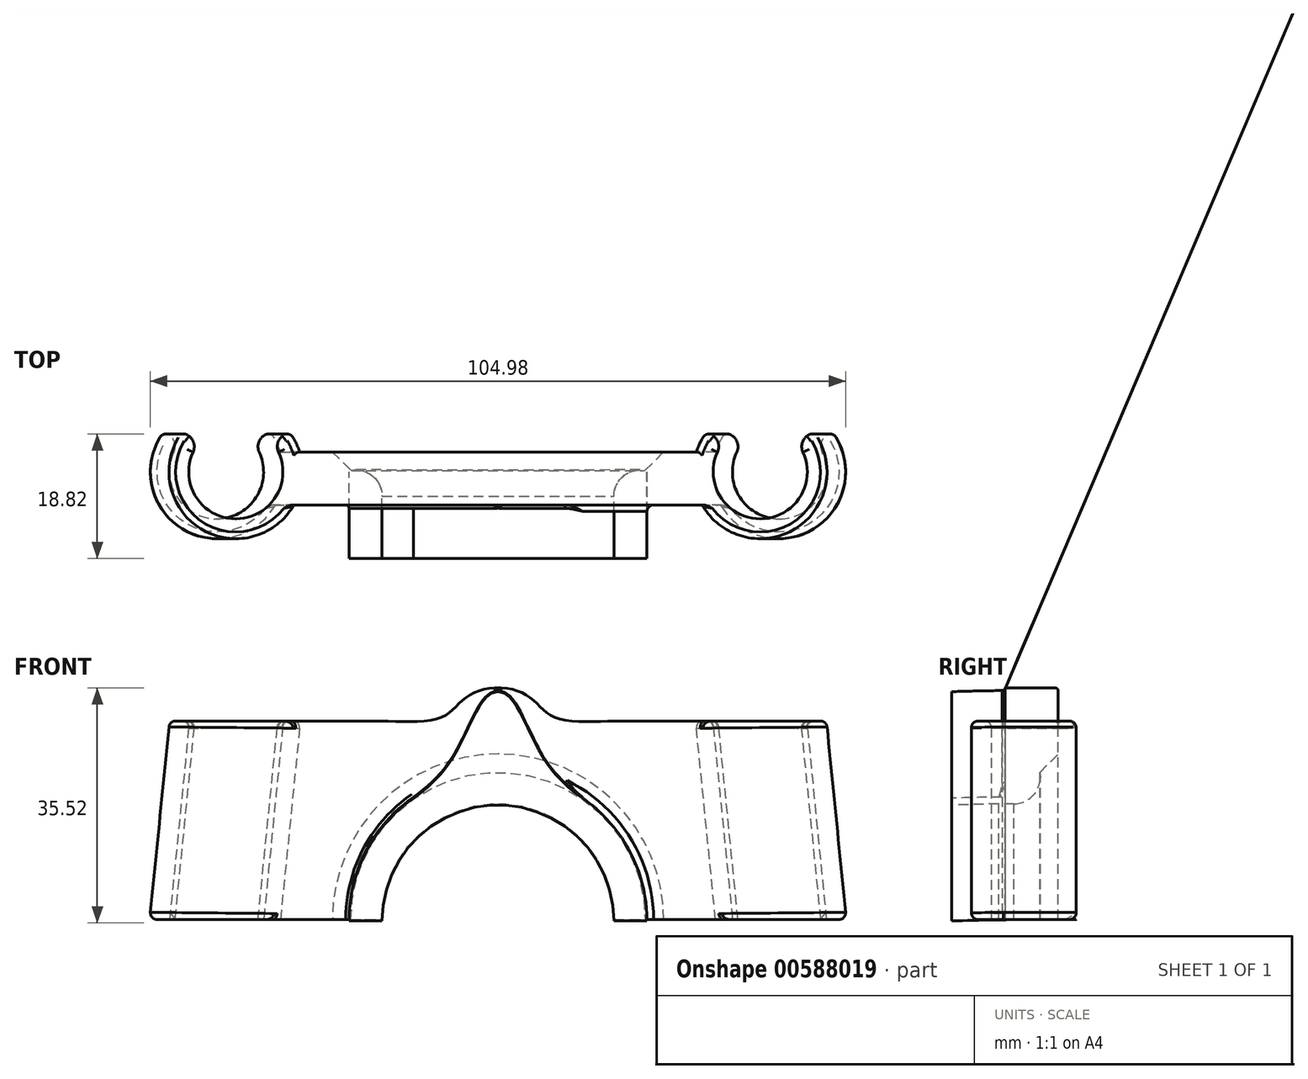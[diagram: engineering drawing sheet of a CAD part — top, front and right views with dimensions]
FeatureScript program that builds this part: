
annotation { "Feature Type Name" : "Feature", "Feature Type Description" : "" }
export const myFeature = defineFeature(function(context is Context, id is Id, definition is map)
    precondition{}
    {
        {
            var Q0;
            Q0=qCreatedBy(makeId("Front.planeOp"),FACE);
            var sketch = newSketch(context, id + "F0", { "sketchPlane" : qUnion([Q0])});
            skLineSegment(sketch, "E0", {"start": v(42.5, 0) * mm, "end": v(39.5, 30) * mm});
            skLineSegment(sketch, "E1", {"start": v(0, 48.67) * mm, "end": v(0, 0) * mm, "construction": true});
            skSolve(sketch);
        }
        {
            var Q0;
            Q0=qCreatedBy(makeId("Top.planeOp"),FACE);
            var sketch = newSketch(context, id + "F1", { "sketchPlane" : qUnion([Q0])});
            skArc(sketch, "E2", {"start": v(36.87, 4.32) * mm, "mid": v(42.5, -7.1) * mm, "end": v(48.13, 4.32) * mm});
            skArc(sketch, "E3.0", {"start": v(34.49, 6.15) * mm, "mid": v(42.5, -10.1) * mm, "end": v(50.51, 6.15) * mm});
            skLineSegment(sketch, "E4", {"start": v(48.13, 4.32) * mm, "end": v(50.51, 6.15) * mm});
            skLineSegment(sketch, "E5", {"start": v(36.87, 4.32) * mm, "end": v(34.49, 6.15) * mm});
            skLineSegment(sketch, "E6", {"start": v(42.5, 0) * mm, "end": v(42.5, 10.1) * mm, "construction": true});
            skLineSegment(sketch, "E7", {"start": v(36.87, 4.32) * mm, "end": v(42.5, 0) * mm, "construction": true});
            skSolve(sketch);
        }
        {
            var Q0;
            Q0 = qSketchRegion(id + "F1", true);
            var Q1;
            Q1=sQuery(id+"F0.wireOp",EDGE,"E0");
            sweep(context, id + "F2", {"profiles" : qUnion([Q0]), "path" : qUnion([Q1]), "keepProfileOrientation" : true});
        }
        {
            var Q0;
            Q0=qCreatedBy(makeId("Right.planeOp"),FACE);
            var sketch = newSketch(context, id + "F3", { "sketchPlane" : qUnion([Q0])});
            skCircle(sketch, "E8", {"center": v(0, -406) * mm, "radius": 406 * mm});
            skSolve(sketch);
        }
        {
            var Q0;
            Q0=makeQuery(id+"F2.opSweep","SWEPT_BODY",BODY,{"disambiguationData":[OSD([sQuery(id+"F0.wireOp",EDGE,"E0"),sQuery(id+"F1.wireOp",EDGE,"E2"),sQuery(id+"F1.wireOp",EDGE,"E3.0"),sQuery(id+"F1.wireOp",EDGE,"E4"),sQuery(id+"F1.wireOp",EDGE,"E5")])]});
            var Q1;
            Q1=qCreatedBy(makeId("Right.planeOp"),FACE);
            mirror(context, id + "F4", {"entities" : qUnion([Q0]), "mirrorPlane" : qUnion([Q1])});
        }
        {
            var Q0;
            Q0=qCreatedBy(makeId("Front.planeOp"),FACE);
            var sketch = newSketch(context, id + "F5", { "sketchPlane" : qUnion([Q0])});
            skArc(sketch, "E9", {"start": v(17.5, 0) * mm, "mid": v(0, 17.5) * mm, "end": v(-17.5, 0) * mm});
            skArc(sketch, "E10.0", {"start": v(22.5, 0) * mm, "mid": v(19.91, 10.48) * mm, "end": v(12.74, 18.54) * mm});
            skLineSegment(sketch, "E11", {"start": v(-22.5, 0) * mm, "end": v(-17.5, 0) * mm});
            skLineSegment(sketch, "E12", {"start": v(17.5, 0) * mm, "end": v(22.5, 0) * mm});
            skFitSpline(sketch, "E13", {"points": [v(12.74, 18.54) * mm, v(6.7, 24.92) * mm, v(2.82, 32.43) * mm, v(0, 34.64) * mm], "startDerivative": vector(-21.82, 15.7) * mm, "endDerivative": vector(-15.88, 1.73) * mm});
            skLineSegment(sketch, "E14", {"start": v(0, 0) * mm, "end": v(0, 35.45) * mm, "construction": true});
            skFitSpline(sketch, "E15.MirrorCS", {"points": [v(-12.74, 18.54) * mm, v(-6.7, 24.92) * mm, v(-2.82, 32.43) * mm, v(0, 34.64) * mm], "startDerivative": vector(21.82, 15.7) * mm, "endDerivative": vector(15.88, 1.73) * mm});
            skArc(sketch, "E16.trimOffspring", {"start": v(-12.74, 18.54) * mm, "mid": v(-19.91, 10.48) * mm, "end": v(-22.5, 0) * mm});
            skSolve(sketch);
        }
        {
            var Q0;
            Q0=qCreatedBy(makeId("Front.planeOp"),FACE);
            var sketch = newSketch(context, id + "F6", { "sketchPlane" : qUnion([Q0])});
            skLineSegment(sketch, "E17", {"start": v(0, 0) * mm, "end": v(0, 43.53) * mm, "construction": true});
            skArc(sketch, "E18", {"start": v(20, 0) * mm, "mid": v(0, 20) * mm, "end": v(-20, 0) * mm});
            skLineSegment(sketch, "E19.MirrorCS", {"start": v(-31.49, 30) * mm, "end": v(-18.64, 30) * mm});
            skFitSpline(sketch, "E20.MirrorCS", {"points": [v(0, 35.01) * mm, v(-5.21, 33.25) * mm, v(-8.7, 30.5) * mm, v(-18.64, 30) * mm], "startDerivative": vector(-19.82, 0.89) * mm, "endDerivative": vector(-23.26, 0) * mm});
            skLineSegment(sketch, "E21.MirrorCS", {"start": v(-34.49, 0) * mm, "end": v(-20, 0) * mm});
            skLineSegment(sketch, "E22.MirrorCS", {"start": v(-34.49, 0) * mm, "end": v(-31.49, 30) * mm});
            skLineSegment(sketch, "E23.MirrorCS", {"start": v(34.49, 0) * mm, "end": v(20, 0) * mm});
            skFitSpline(sketch, "E24.MirrorCS", {"points": [v(0, 35.01) * mm, v(5.21, 33.25) * mm, v(8.7, 30.5) * mm, v(18.64, 30) * mm], "startDerivative": vector(19.82, 0.89) * mm, "endDerivative": vector(23.26, 0) * mm});
            skLineSegment(sketch, "E25.MirrorCS", {"start": v(34.49, 0) * mm, "end": v(31.49, 30) * mm});
            skLineSegment(sketch, "E26.MirrorCS", {"start": v(31.49, 30) * mm, "end": v(18.64, 30) * mm});
            skSolve(sketch);
        }
        {
            var Q0;
            Q0 = qSketchRegion(id + "F6", true);
            extrude(context, id + "F7", {"entities" : qUnion([Q0]), "operationType" : NewBodyOperationType.ADD, "depth" : 5 * mm, "offsetDistance" : 25 * mm, "hasSecondDirection" : true, "secondDirectionOppositeDirection" : true, "secondDirectionDepth" : 3 * mm});
        }
        {
            var Q0;
            Q0=makeQuery(id+"F5.imprint","IMPRINT",FACE,{"disambiguationData":[TD([[makeQuery(id+"F5.imprint","IMPRINT",EDGE,{"derivedFrom":sQuery(id+"F5.wireOp",EDGE,"E9")}),-1.0]])]});
            var Q1;
            Q1=sQuery(id+"F3.wireOp",EDGE,"E8");
            revolve(context, id + "F8", {"operationType" : NewBodyOperationType.ADD, "entities" : qUnion([Q0]), "axis" : qUnion([Q1]), "revolveType" : RevolveType.ONE_DIRECTION, "angle" : 40 * degree});
        }
        {
            var Q0;
            Q0=makeQuery(id+"F8.opRevolve","CAP_EDGE",EDGE,{"disambiguationData":[OSD([sQuery(id+"F5.wireOp",EDGE,"E11")])],"isStart":false});
            chamfer(context, id + "F9", {"entities" : qUnion([Q0]), "width" : 30 * mm, "tangentPropagation" : true});
        }
        {
            var Q0;
            Q0=makeQuery(id+"F8.opRevolve","CAP_EDGE",EDGE,{"disambiguationData":[OSD([sQuery(id+"F5.wireOp",EDGE,"E9")])],"isStart":false});
            var Q1;
            Q1=makeQuery(id+"F8.opRevolve","CAP_EDGE",EDGE,{"disambiguationData":[OSD([sQuery(id+"F5.wireOp",EDGE,"E9")])],"isStart":true});
            fillet(context, id + "F10", {"entities" : qUnion([Q0, Q1]), "radius" : 4 * mm, "tangentPropagation" : true, "allowEdgeOverflow" : false});
        }
        {
            var Q0;
            Q0=makeQuery(id+"F2.opSweep","SWEPT_EDGE",EDGE,{"disambiguationData":[OSD([sQuery(id+"F0.wireOp",EDGE,"E0"),sQuery(id+"F1.wireOp",EDGE,"E2"),sQuery(id+"F1.wireOp",EDGE,"E5")])]});
            var Q1;
            Q1=makeQuery(id+"F2.opSweep","SWEPT_EDGE",EDGE,{"disambiguationData":[OSD([sQuery(id+"F0.wireOp",EDGE,"E0"),sQuery(id+"F1.wireOp",EDGE,"E2"),sQuery(id+"F1.wireOp",EDGE,"E4")])]});
            var Q2;
            Q2=makeQuery(id+"F4.opPattern","COPY",EDGE,{"derivedFrom":makeQuery(id+"F2.opSweep","SWEPT_EDGE",EDGE,{"disambiguationData":[OSD([sQuery(id+"F0.wireOp",EDGE,"E0"),sQuery(id+"F1.wireOp",EDGE,"E2"),sQuery(id+"F1.wireOp",EDGE,"E4")])]}),"instanceName":"1"});
            var Q3;
            Q3=makeQuery(id+"F4.opPattern","COPY",EDGE,{"derivedFrom":makeQuery(id+"F2.opSweep","SWEPT_EDGE",EDGE,{"disambiguationData":[OSD([sQuery(id+"F0.wireOp",EDGE,"E0"),sQuery(id+"F1.wireOp",EDGE,"E2"),sQuery(id+"F1.wireOp",EDGE,"E5")])]}),"instanceName":"1"});
            fillet(context, id + "F11", {"entities" : qUnion([Q0, Q1, Q2, Q3]), "radius" : 2 * mm, "tangentPropagation" : true, "allowEdgeOverflow" : false});
        }
        {
            var Q0;
            {var subQ1=sQuery(id+"F1.wireOp",EDGE,"E4");var subQ2=sQuery(id+"F0.wireOp",EDGE,"E0");var subQ3=sQuery(id+"F1.wireOp",EDGE,"E3.0");var subQ4=sQuery(id+"F0.wireOp",VERTEX,"E0.end");Q0=makeQuery(id+"F7.boolean.opBoolean","SPLIT",EDGE,{"disambiguationData":[TD([makeQuery(id+"F4.opPattern","COPY",FACE,{"derivedFrom":makeQuery(id+"F2.opSweep","SWEPT_FACE",FACE,{"disambiguationData":[OSD([subQ2,subQ1])]}),"instanceName":"1"})])],"derivedFrom":makeQuery(id+"F4.opPattern","COPY",EDGE,{"derivedFrom":makeQuery(id+"F2.opSweep","CAP_EDGE",EDGE,{"disambiguationData":[OSD([subQ4,subQ3])],"isStart":false}),"instanceName":"1"})});}
            var Q1;
            {var subQ0=sQuery(id+"F1.wireOp",EDGE,"E5");var subQ1=sQuery(id+"F0.wireOp",EDGE,"E0");var subQ2=sQuery(id+"F1.wireOp",EDGE,"E2");var subQ5=sQuery(id+"F1.wireOp",EDGE,"E4");var subQ6=sQuery(id+"F0.wireOp",VERTEX,"E0.end");var subQ9=makeQuery(id+"F4.opPattern","COPY",EDGE,{"derivedFrom":makeQuery(id+"F2.opSweep","CAP_EDGE",EDGE,{"disambiguationData":[OSD([subQ6,subQ2])],"isStart":false}),"instanceName":"1"});Q1=makeQuery(id+"Fb2eIdGMMGndcXa_1.opDeleteFace","MERGE",EDGE,{"derivedFrom":[makeQuery(id+"F7.boolean.opBoolean","SPLIT",EDGE,{"disambiguationData":[TD([makeQuery(id+"F4.opPattern","COPY",FACE,{"derivedFrom":makeQuery(id+"F2.opSweep","SWEPT_FACE",FACE,{"disambiguationData":[OSD([subQ1,subQ5])]}),"instanceName":"1"})])],"derivedFrom":subQ9}),makeQuery(id+"F7.boolean.opBoolean","SPLIT",EDGE,{"disambiguationData":[TD([makeQuery(id+"F4.opPattern","COPY",FACE,{"derivedFrom":makeQuery(id+"F2.opSweep","SWEPT_FACE",FACE,{"disambiguationData":[OSD([subQ1,subQ0])]}),"instanceName":"1"})])],"derivedFrom":subQ9})]});}
            var Q2;
            {var subQ0=sQuery(id+"F1.wireOp",EDGE,"E5");var subQ1=sQuery(id+"F0.wireOp",EDGE,"E0");var subQ2=sQuery(id+"F1.wireOp",EDGE,"E3.0");var subQ4=sQuery(id+"F0.wireOp",VERTEX,"E0.end");Q2=makeQuery(id+"F7.boolean.opBoolean","SPLIT",EDGE,{"disambiguationData":[TD([makeQuery(id+"F4.opPattern","COPY",FACE,{"derivedFrom":makeQuery(id+"F2.opSweep","SWEPT_FACE",FACE,{"disambiguationData":[OSD([subQ1,subQ0])]}),"instanceName":"1"})])],"derivedFrom":makeQuery(id+"F4.opPattern","COPY",EDGE,{"derivedFrom":makeQuery(id+"F2.opSweep","CAP_EDGE",EDGE,{"disambiguationData":[OSD([subQ4,subQ2])],"isStart":false}),"instanceName":"1"})});}
            var Q3;
            Q3=makeQuery(id+"F4.opPattern","COPY",EDGE,{"derivedFrom":makeQuery(id+"F2.opSweep","SWEPT_EDGE",EDGE,{"disambiguationData":[OSD([sQuery(id+"F0.wireOp",EDGE,"E0"),sQuery(id+"F1.wireOp",EDGE,"E3.0"),sQuery(id+"F1.wireOp",EDGE,"E4")])]}),"instanceName":"1"});
            var Q4;
            Q4=makeQuery(id+"F4.opPattern","COPY",EDGE,{"derivedFrom":makeQuery(id+"F2.opSweep","SWEPT_EDGE",EDGE,{"disambiguationData":[OSD([sQuery(id+"F0.wireOp",EDGE,"E0"),sQuery(id+"F1.wireOp",EDGE,"E3.0"),sQuery(id+"F1.wireOp",EDGE,"E5")])]}),"instanceName":"1"});
            var Q5;
            {var subQ0=sQuery(id+"F1.wireOp",EDGE,"E5");var subQ1=sQuery(id+"F0.wireOp",EDGE,"E0");var subQ2=sQuery(id+"F1.wireOp",EDGE,"E2");var subQ5=sQuery(id+"F1.wireOp",EDGE,"E4");var subQ6=sQuery(id+"F0.wireOp",VERTEX,"E0.end");var subQ9=makeQuery(id+"F2.opSweep","CAP_EDGE",EDGE,{"disambiguationData":[OSD([subQ6,subQ2])],"isStart":false});Q5=makeQuery(id+"FDVgIl0iVr0qq6Z_1.opDeleteFace","MERGE",EDGE,{"derivedFrom":[makeQuery(id+"F7.boolean.opBoolean","SPLIT",EDGE,{"disambiguationData":[TD([makeQuery(id+"F2.opSweep","SWEPT_FACE",FACE,{"disambiguationData":[OSD([subQ1,subQ5])]})])],"derivedFrom":subQ9}),makeQuery(id+"F7.boolean.opBoolean","SPLIT",EDGE,{"disambiguationData":[TD([makeQuery(id+"F2.opSweep","SWEPT_FACE",FACE,{"disambiguationData":[OSD([subQ1,subQ0])]})])],"derivedFrom":subQ9})]});}
            var Q6;
            Q6=makeQuery(id+"F2.opSweep","SWEPT_EDGE",EDGE,{"disambiguationData":[OSD([sQuery(id+"F0.wireOp",EDGE,"E0"),sQuery(id+"F1.wireOp",EDGE,"E3.0"),sQuery(id+"F1.wireOp",EDGE,"E5")])]});
            var Q7;
            {var subQ1=sQuery(id+"F1.wireOp",EDGE,"E5");var subQ2=sQuery(id+"F0.wireOp",EDGE,"E0");var subQ3=sQuery(id+"F1.wireOp",EDGE,"E3.0");var subQ4=sQuery(id+"F0.wireOp",VERTEX,"E0.end");Q7=makeQuery(id+"F7.boolean.opBoolean","SPLIT",EDGE,{"disambiguationData":[TD([makeQuery(id+"F2.opSweep","SWEPT_FACE",FACE,{"disambiguationData":[OSD([subQ2,subQ1])]})])],"derivedFrom":makeQuery(id+"F2.opSweep","CAP_EDGE",EDGE,{"disambiguationData":[OSD([subQ4,subQ3])],"isStart":false})});}
            var Q8;
            {var subQ1=sQuery(id+"F1.wireOp",EDGE,"E4");var subQ2=sQuery(id+"F1.wireOp",EDGE,"E3.0");var subQ3=sQuery(id+"F0.wireOp",VERTEX,"E0.end");var subQ4=sQuery(id+"F0.wireOp",EDGE,"E0");Q8=makeQuery(id+"F7.boolean.opBoolean","SPLIT",EDGE,{"disambiguationData":[TD([makeQuery(id+"F2.opSweep","SWEPT_FACE",FACE,{"disambiguationData":[OSD([subQ4,subQ1])]})])],"derivedFrom":makeQuery(id+"F2.opSweep","CAP_EDGE",EDGE,{"disambiguationData":[OSD([subQ3,subQ2])],"isStart":false})});}
            var Q9;
            Q9=makeQuery(id+"F2.opSweep","SWEPT_EDGE",EDGE,{"disambiguationData":[OSD([sQuery(id+"F0.wireOp",EDGE,"E0"),sQuery(id+"F1.wireOp",EDGE,"E3.0"),sQuery(id+"F1.wireOp",EDGE,"E4")])]});
            fillet(context, id + "F12", {"entities" : qUnion([Q0, Q1, Q2, Q3, Q4, Q5, Q6, Q7, Q8, Q9]), "radius" : 1 * mm, "tangentPropagation" : true, "allowEdgeOverflow" : false});
        }
        {
            var Q0;
            {var subQ0=sQuery(id+"F1.wireOp",EDGE,"E4");var subQ1=sQuery(id+"F0.wireOp",EDGE,"E0");var subQ2=sQuery(id+"F1.wireOp",EDGE,"E3.0");var subQ4=sQuery(id+"F0.wireOp",VERTEX,"E0.start");Q0=makeQuery(id+"F7.boolean.opBoolean","SPLIT",EDGE,{"disambiguationData":[TD([makeQuery(id+"F2.opSweep","SWEPT_FACE",FACE,{"disambiguationData":[OSD([subQ1,subQ0])]})])],"derivedFrom":makeQuery(id+"F2.opSweep","CAP_EDGE",EDGE,{"disambiguationData":[OSD([subQ4,subQ2])],"isStart":true})});}
            var Q1;
            Q1=makeQuery(id+"F2.opSweep","CAP_EDGE",EDGE,{"disambiguationData":[OSD([sQuery(id+"F0.wireOp",VERTEX,"E0.start"),sQuery(id+"F1.wireOp",EDGE,"E4")])],"isStart":true});
            var Q2;
            {var subQ1=sQuery(id+"F1.wireOp",EDGE,"E4");var subQ2=sQuery(id+"F1.wireOp",EDGE,"E3.0");var subQ3=sQuery(id+"F0.wireOp",VERTEX,"E0.start");var subQ4=sQuery(id+"F0.wireOp",EDGE,"E0");Q2=makeQuery(id+"F7.boolean.opBoolean","SPLIT",EDGE,{"disambiguationData":[TD([makeQuery(id+"F4.opPattern","COPY",FACE,{"derivedFrom":makeQuery(id+"F2.opSweep","SWEPT_FACE",FACE,{"disambiguationData":[OSD([subQ4,subQ1])]}),"instanceName":"1"})])],"derivedFrom":makeQuery(id+"F4.opPattern","COPY",EDGE,{"derivedFrom":makeQuery(id+"F2.opSweep","CAP_EDGE",EDGE,{"disambiguationData":[OSD([subQ3,subQ2])],"isStart":true}),"instanceName":"1"})});}
            var Q3;
            Q3=makeQuery(id+"F4.opPattern","COPY",EDGE,{"derivedFrom":makeQuery(id+"F2.opSweep","CAP_EDGE",EDGE,{"disambiguationData":[OSD([sQuery(id+"F0.wireOp",VERTEX,"E0.start"),sQuery(id+"F1.wireOp",EDGE,"E4")])],"isStart":true}),"instanceName":"1"});
            var Q4;
            Q4=makeQuery(id+"F8.boolean.opBoolean","INTERSECT",EDGE,{"derivedFrom":[makeQuery(id+"F7.opExtrude","CAP_FACE",FACE,{"disambiguationData":[OSD([sQuery(id+"F6.wireOp",EDGE,"a6a3b8ac-eb5a-4d4e-b9e6-10557efb4ea6"),sQuery(id+"F6.wireOp",EDGE,"13889ff9-7ed8-4a99-b5cb-801a0fdd9943.0"),sQuery(id+"F6.wireOp",EDGE,"UqJnl0P3-Wh1s-lfIW-4dyv-xBbzbC0pXPwb"),sQuery(id+"F6.wireOp",EDGE,"E18"),sQuery(id+"F6.wireOp",EDGE,"E19.MirrorCS"),sQuery(id+"F6.wireOp",EDGE,"E20.MirrorCS"),sQuery(id+"F6.wireOp",EDGE,"fJR0S3g4-zIrf-VDX3-eyqh-DodSpAN4tFm6"),sQuery(id+"F6.wireOp",EDGE,"E21.MirrorCS"),sQuery(id+"F6.wireOp",EDGE,"E22.MirrorCS")])],"isStart":false}),makeQuery(id+"F8.opRevolve","SWEPT_FACE",FACE,{"disambiguationData":[OSD([sQuery(id+"F5.wireOp",EDGE,"E10.0")])]})]});
            var Q5;
            Q5=makeQuery(id+"F7.opExtrude","SWEPT_EDGE",EDGE,{"disambiguationData":[OSD([sQuery(id+"F6.wireOp",EDGE,"E20.MirrorCS"),sQuery(id+"F6.wireOp",EDGE,"E24.MirrorCS")])]});
            var Q6;
            Q6=makeQuery(id+"F8.opRevolve","SWEPT_EDGE",EDGE,{"disambiguationData":[OSD([sQuery(id+"F5.wireOp",EDGE,"E13"),sQuery(id+"F5.wireOp",EDGE,"E15.MirrorCS")])]});
            fillet(context, id + "F13", {"entities" : qUnion([Q0, Q1, Q2, Q3, Q4, Q5, Q6]), "radius" : 1 * mm, "allowEdgeOverflow" : false});
        }
        {
            var Q0;
            Q0=makeQuery(id+"F9.opChamfer","BLEND_EDGE",EDGE,{"blendedFrom":[makeQuery(id+"F8.opRevolve","CAP_EDGE",EDGE,{"disambiguationData":[OSD([sQuery(id+"F5.wireOp",EDGE,"E11")])],"isStart":false}),makeQuery(id+"F8.opRevolve","SWEPT_FACE",FACE,{"disambiguationData":[OSD([sQuery(id+"F5.wireOp",EDGE,"E15.MirrorCS")])]})],"blendedInto":[makeQuery(id+"F8.opRevolve","SWEPT_FACE",FACE,{"disambiguationData":[OSD([sQuery(id+"F5.wireOp",EDGE,"E15.MirrorCS")])]})]});
            var Q1;
            {var subQ0=sQuery(id+"F5.wireOp",EDGE,"E11");Q1=makeQuery(id+"F9.opChamfer","BLEND_EDGE",EDGE,{"blendedFrom":[makeQuery(id+"F8.opRevolve","CAP_EDGE",EDGE,{"disambiguationData":[OSD([subQ0])],"isStart":false}),makeQuery(id+"F8.opRevolve","CAP_FACE",FACE,{"disambiguationData":[OSD([sQuery(id+"F5.wireOp",EDGE,"E9"),sQuery(id+"F5.wireOp",EDGE,"E10.0"),subQ0,sQuery(id+"F5.wireOp",EDGE,"E12"),sQuery(id+"F5.wireOp",EDGE,"E13"),sQuery(id+"F5.wireOp",EDGE,"E15.MirrorCS"),sQuery(id+"F5.wireOp",EDGE,"E16.trimOffspring")])],"isStart":false})],"blendedInto":[makeQuery(id+"F8.opRevolve","CAP_FACE",FACE,{"disambiguationData":[OSD([sQuery(id+"F5.wireOp",EDGE,"E9"),sQuery(id+"F5.wireOp",EDGE,"E10.0"),subQ0,sQuery(id+"F5.wireOp",EDGE,"E12"),sQuery(id+"F5.wireOp",EDGE,"E13"),sQuery(id+"F5.wireOp",EDGE,"E15.MirrorCS"),sQuery(id+"F5.wireOp",EDGE,"E16.trimOffspring")])],"isStart":false})]});}
            var Q2;
            Q2=makeQuery(id+"F9.opChamfer","BLEND_EDGE",EDGE,{"blendedFrom":[makeQuery(id+"F8.opRevolve","CAP_EDGE",EDGE,{"disambiguationData":[OSD([sQuery(id+"F5.wireOp",EDGE,"E11")])],"isStart":false}),makeQuery(id+"F8.opRevolve","SWEPT_FACE",FACE,{"disambiguationData":[OSD([sQuery(id+"F5.wireOp",EDGE,"E13")])]})],"blendedInto":[makeQuery(id+"F8.opRevolve","SWEPT_FACE",FACE,{"disambiguationData":[OSD([sQuery(id+"F5.wireOp",EDGE,"E13")])]})]});
            var Q3;
            Q3=makeQuery(id+"F8.opRevolve","CAP_EDGE",EDGE,{"disambiguationData":[OSD([sQuery(id+"F5.wireOp",EDGE,"E15.MirrorCS")])],"isStart":false});
            var Q4;
            Q4=makeQuery(id+"F9.opChamfer","BLEND_EDGE",EDGE,{"blendedFrom":[makeQuery(id+"F8.opRevolve","CAP_EDGE",EDGE,{"disambiguationData":[OSD([sQuery(id+"F5.wireOp",EDGE,"E11")])],"isStart":false}),makeQuery(id+"F8.opRevolve","SWEPT_FACE",FACE,{"disambiguationData":[OSD([sQuery(id+"F5.wireOp",EDGE,"E16.trimOffspring")])]})],"blendedInto":[makeQuery(id+"F8.opRevolve","SWEPT_FACE",FACE,{"disambiguationData":[OSD([sQuery(id+"F5.wireOp",EDGE,"E16.trimOffspring")])]})]});
            var Q5;
            Q5=makeQuery(id+"F9.opChamfer","BLEND_EDGE",EDGE,{"blendedFrom":[makeQuery(id+"F8.opRevolve","CAP_EDGE",EDGE,{"disambiguationData":[OSD([sQuery(id+"F5.wireOp",EDGE,"E11")])],"isStart":false}),makeQuery(id+"F8.opRevolve","SWEPT_FACE",FACE,{"disambiguationData":[OSD([sQuery(id+"F5.wireOp",EDGE,"E10.0")])]})],"blendedInto":[makeQuery(id+"F8.opRevolve","SWEPT_FACE",FACE,{"disambiguationData":[OSD([sQuery(id+"F5.wireOp",EDGE,"E10.0")])]})]});
            var Q6;
            {var subQ0=sQuery(id+"F5.wireOp",EDGE,"E11");Q6=makeQuery(id+"F9.opChamfer","BLEND_EDGE",EDGE,{"blendedFrom":[makeQuery(id+"F8.opRevolve","CAP_EDGE",EDGE,{"disambiguationData":[OSD([subQ0])],"isStart":false}),makeQuery(id+"F8.opRevolve","SWEPT_FACE",FACE,{"disambiguationData":[OSD([subQ0])]})],"blendedInto":[makeQuery(id+"F8.opRevolve","SWEPT_FACE",FACE,{"disambiguationData":[OSD([subQ0])]})]});}
            var Q7;
            Q7=makeQuery(id+"F9.opChamfer","BLEND_EDGE",EDGE,{"blendedFrom":[makeQuery(id+"F8.opRevolve","CAP_EDGE",EDGE,{"disambiguationData":[OSD([sQuery(id+"F5.wireOp",EDGE,"E11")])],"isStart":false}),makeQuery(id+"F8.opRevolve","SWEPT_FACE",FACE,{"disambiguationData":[OSD([sQuery(id+"F5.wireOp",EDGE,"E12")])]})],"blendedInto":[makeQuery(id+"F8.opRevolve","SWEPT_FACE",FACE,{"disambiguationData":[OSD([sQuery(id+"F5.wireOp",EDGE,"E12")])]})]});
            fillet(context, id + "F14", {"entities" : qUnion([Q0, Q1, Q2, Q3, Q4, Q5, Q6, Q7]), "radius" : .9 * mm, "tangentPropagation" : true, "allowEdgeOverflow" : false});
        }
        {
            var Q0;
            Q0=makeQuery(id+"F7.opExtrude","CAP_EDGE",EDGE,{"disambiguationData":[OSD([sQuery(id+"F6.wireOp",EDGE,"E18")])],"isStart":true});
            chamfer(context, id + "F15", {"entities" : qUnion([Q0]), "width" : 5 * mm, "tangentPropagation" : true});
        }
        {
            var Q0;
            Q0=makeQuery(id+"F8.boolean.opBoolean","INTERSECT",EDGE,{"derivedFrom":[makeQuery(id+"F7.opExtrude","CAP_FACE",FACE,{"disambiguationData":[OSD([sQuery(id+"F6.wireOp",EDGE,"E18"),sQuery(id+"F6.wireOp",EDGE,"E19.MirrorCS"),sQuery(id+"F6.wireOp",EDGE,"E20.MirrorCS"),sQuery(id+"F6.wireOp",EDGE,"E21.MirrorCS"),sQuery(id+"F6.wireOp",EDGE,"E22.MirrorCS"),sQuery(id+"F6.wireOp",EDGE,"E23.MirrorCS"),sQuery(id+"F6.wireOp",EDGE,"E24.MirrorCS"),sQuery(id+"F6.wireOp",EDGE,"E25.MirrorCS"),sQuery(id+"F6.wireOp",EDGE,"E26.MirrorCS")])],"isStart":false}),makeQuery(id+"F8.opRevolve","SWEPT_FACE",FACE,{"disambiguationData":[OSD([sQuery(id+"F5.wireOp",EDGE,"E13")])]})]});
            var Q1;
            Q1=makeQuery(id+"F7.opExtrude","CAP_EDGE",EDGE,{"disambiguationData":[OSD([sQuery(id+"F6.wireOp",EDGE,"E24.MirrorCS")])],"isStart":true});
            var Q2;
            Q2=makeQuery(id+"F7.boolean.opBoolean","INTERSECT",EDGE,{"derivedFrom":[makeQuery(id+"F2.opSweep","SWEPT_FACE",FACE,{"disambiguationData":[OSD([sQuery(id+"F0.wireOp",EDGE,"E0"),sQuery(id+"F1.wireOp",EDGE,"E3.0")])]}),makeQuery(id+"F7.opExtrude","CAP_FACE",FACE,{"disambiguationData":[OSD([sQuery(id+"F6.wireOp",EDGE,"E18"),sQuery(id+"F6.wireOp",EDGE,"E19.MirrorCS"),sQuery(id+"F6.wireOp",EDGE,"E20.MirrorCS"),sQuery(id+"F6.wireOp",EDGE,"E21.MirrorCS"),sQuery(id+"F6.wireOp",EDGE,"E22.MirrorCS"),sQuery(id+"F6.wireOp",EDGE,"E23.MirrorCS"),sQuery(id+"F6.wireOp",EDGE,"E24.MirrorCS"),sQuery(id+"F6.wireOp",EDGE,"E25.MirrorCS"),sQuery(id+"F6.wireOp",EDGE,"E26.MirrorCS")])],"isStart":false})]});
            var Q3;
            Q3=makeQuery(id+"F7.boolean.opBoolean","INTERSECT",EDGE,{"derivedFrom":[makeQuery(id+"F4.opPattern","COPY",FACE,{"derivedFrom":makeQuery(id+"F2.opSweep","SWEPT_FACE",FACE,{"disambiguationData":[OSD([sQuery(id+"F0.wireOp",EDGE,"E0"),sQuery(id+"F1.wireOp",EDGE,"E3.0")])]}),"instanceName":"1"}),makeQuery(id+"F7.opExtrude","CAP_FACE",FACE,{"disambiguationData":[OSD([sQuery(id+"F6.wireOp",EDGE,"E18"),sQuery(id+"F6.wireOp",EDGE,"E19.MirrorCS"),sQuery(id+"F6.wireOp",EDGE,"E20.MirrorCS"),sQuery(id+"F6.wireOp",EDGE,"E21.MirrorCS"),sQuery(id+"F6.wireOp",EDGE,"E22.MirrorCS"),sQuery(id+"F6.wireOp",EDGE,"E23.MirrorCS"),sQuery(id+"F6.wireOp",EDGE,"E24.MirrorCS"),sQuery(id+"F6.wireOp",EDGE,"E25.MirrorCS"),sQuery(id+"F6.wireOp",EDGE,"E26.MirrorCS")])],"isStart":false})]});
            fillet(context, id + "F16", {"entities" : qUnion([Q0, Q1, Q2, Q3]), "radius" : .5 * mm, "tangentPropagation" : true, "allowEdgeOverflow" : false});
        }
        {
            var Q0;
            Q0=qCreatedBy(makeId("Right.planeOp"),FACE);
            var sketch = newSketch(context, id + "F17", { "sketchPlane" : qUnion([Q0])});
            skLineSegment(sketch, "E27.bottom", {"start": v(-286.5, 45.7) * mm, "end": v(-13.1, 45.7) * mm});
            skLineSegment(sketch, "E27.top", {"start": v(-286.5, -94.48) * mm, "end": v(-13.1, -94.48) * mm});
            skLineSegment(sketch, "E27.left", {"start": v(-286.5, 45.7) * mm, "end": v(-286.5, -94.48) * mm});
            skLineSegment(sketch, "E27.right", {"start": v(-13.1, 45.7) * mm, "end": v(-13.1, -94.48) * mm});
            skSolve(sketch);
        }
        {
            var Q0;
            Q0 = qSketchRegion(id + "F17", true);
            extrude(context, id + "F18", {"entities" : qUnion([Q0]), "operationType" : NewBodyOperationType.REMOVE, "endBound" : BoundingType.THROUGH_ALL, "oppositeDirection" : true, "depth" : 25 * mm, "offsetDistance" : 25 * mm, "hasSecondDirection" : true, "secondDirectionBound" : SecondDirectionBoundingType.THROUGH_ALL, "secondDirectionOppositeDirection" : false, "secondDirectionDepth" : 25 * mm});
        }
    });
